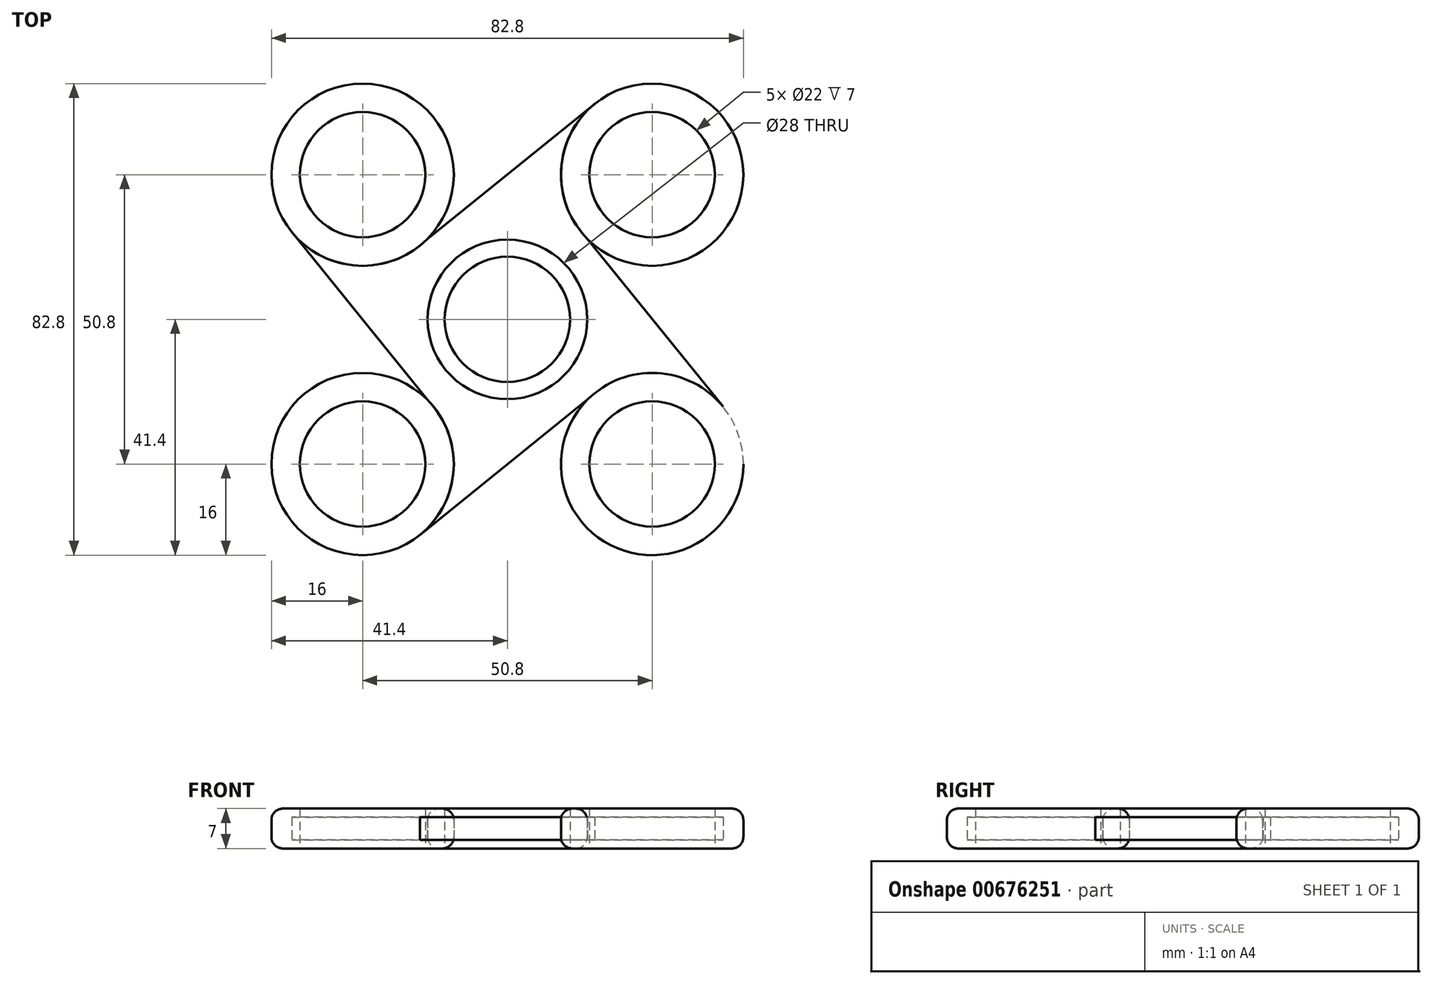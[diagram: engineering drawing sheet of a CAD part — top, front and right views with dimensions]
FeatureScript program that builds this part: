
annotation { "Feature Type Name" : "Feature", "Feature Type Description" : "" }
export const myFeature = defineFeature(function(context is Context, id is Id, definition is map)
    precondition{}
    {
        {
            var Q0;
            Q0=qCreatedBy(makeId("Top.planeOp"),FACE);
            var sketch = newSketch(context, id + "F0", { "sketchPlane" : qUnion([Q0])});
            skLineSegment(sketch, "E0.bottom", {"start": v(0, 0) * mm, "end": v(50.8, 0) * mm, "construction": true});
            skLineSegment(sketch, "E0.top", {"start": v(0, -50.8) * mm, "end": v(50.8, -50.8) * mm, "construction": true});
            skLineSegment(sketch, "E0.left", {"start": v(0, 0) * mm, "end": v(0, -50.8) * mm, "construction": true});
            skLineSegment(sketch, "E0.right", {"start": v(50.8, 0) * mm, "end": v(50.8, -50.8) * mm, "construction": true});
            skCircle(sketch, "E1", {"center": v(0, 0) * mm, "radius": 11 * mm});
            skCircle(sketch, "E2", {"center": v(50.8, 0) * mm, "radius": 11 * mm});
            skCircle(sketch, "E3", {"center": v(50.8, -50.8) * mm, "radius": 11 * mm});
            skCircle(sketch, "E4", {"center": v(0, -50.8) * mm, "radius": 11 * mm});
            skCircle(sketch, "E5", {"center": v(0, -50.8) * mm, "radius": 4 * mm});
            skCircle(sketch, "E6", {"center": v(0, 0) * mm, "radius": 4 * mm});
            skCircle(sketch, "E7", {"center": v(50.8, 0) * mm, "radius": 4 * mm});
            skCircle(sketch, "E8", {"center": v(50.8, -50.8) * mm, "radius": 4 * mm});
            skLineSegment(sketch, "E9", {"start": v(0, -50.8) * mm, "end": v(50.8, 0) * mm, "construction": true});
            skLineSegment(sketch, "E10", {"start": v(50.8, -50.8) * mm, "end": v(0, 0) * mm, "construction": true});
            skCircle(sketch, "E11", {"center": v(25.4, -25.4) * mm, "radius": 4 * mm});
            skCircle(sketch, "E12", {"center": v(25.4, -25.4) * mm, "radius": 11 * mm});
            skCircle(sketch, "E13", {"center": v(0, 0) * mm, "radius": 16 * mm});
            skCircle(sketch, "E14", {"center": v(50.8, 0) * mm, "radius": 16 * mm});
            skCircle(sketch, "E15", {"center": v(50.8, -50.8) * mm, "radius": 16 * mm});
            skCircle(sketch, "E16", {"center": v(0, -50.8) * mm, "radius": 16 * mm});
            skLineSegment(sketch, "E17", {"start": v(11.31, -11.31) * mm, "end": v(40.75, 12.45) * mm});
            skLineSegment(sketch, "E18", {"start": v(40.75, 12.45) * mm, "end": v(50.8, 0) * mm});
            skLineSegment(sketch, "E19", {"start": v(39.49, -11.31) * mm, "end": v(63.25, -40.75) * mm});
            skLineSegment(sketch, "E20", {"start": v(63.25, -40.75) * mm, "end": v(50.8, -50.8) * mm});
            skLineSegment(sketch, "E21", {"start": v(39.49, -39.49) * mm, "end": v(10.05, -63.25) * mm});
            skLineSegment(sketch, "E22", {"start": v(10.05, -63.25) * mm, "end": v(0, -50.8) * mm});
            skLineSegment(sketch, "E23", {"start": v(11.31, -39.49) * mm, "end": v(-12.45, -10.05) * mm});
            skLineSegment(sketch, "E24", {"start": v(-12.45, -10.05) * mm, "end": v(0, 0) * mm});
            skCircle(sketch, "E25", {"center": v(25.4, -25.4) * mm, "radius": 14 * mm});
            skSolve(sketch);
        }
        {
            var Q0;
            {var subQ5=sQuery(id+"F0.wireOp",EDGE,"E17");Q0=makeQuery(id+"F0.imprint","IMPRINT",FACE,{"disambiguationData":[TD([[makeQuery(id+"F0.imprint","IMPRINT",EDGE,{"derivedFrom":subQ5}),-1.0]])]});}
            extrude(context, id + "F1", {"entities" : qUnion([Q0]), "endBound" : BoundingType.SYMMETRIC, "depth" : 4 * mm, "offsetDistance" : 25 * mm});
        }
        {
            var Q0;
            Q0=makeQuery(id+"F0.imprint","IMPRINT",FACE,{"disambiguationData":[TD([[makeQuery(id+"F0.imprint","IMPRINT",EDGE,{"derivedFrom":sQuery(id+"F0.wireOp",EDGE,"E4")}),-1.0]])]});
            var Q1;
            Q1=makeQuery(id+"F0.imprint","IMPRINT",FACE,{"disambiguationData":[TD([[makeQuery(id+"F0.imprint","IMPRINT",EDGE,{"derivedFrom":sQuery(id+"F0.wireOp",EDGE,"E3")}),-1.0]])]});
            var Q2;
            Q2=makeQuery(id+"F0.imprint","IMPRINT",FACE,{"disambiguationData":[TD([[makeQuery(id+"F0.imprint","IMPRINT",EDGE,{"derivedFrom":sQuery(id+"F0.wireOp",EDGE,"E2")}),-1.0]])]});
            var Q3;
            Q3=makeQuery(id+"F0.imprint","IMPRINT",FACE,{"disambiguationData":[TD([[makeQuery(id+"F0.imprint","IMPRINT",EDGE,{"derivedFrom":sQuery(id+"F0.wireOp",EDGE,"E1")}),-1.0]])]});
            extrude(context, id + "F2", {"entities" : qUnion([Q0, Q1, Q2, Q3]), "endBound" : BoundingType.SYMMETRIC, "depth" : 7 * mm, "offsetDistance" : 25 * mm});
        }
        {
            var Q0;
            Q0=makeQuery(id+"F0.imprint","IMPRINT",FACE,{"disambiguationData":[TD([[makeQuery(id+"F0.imprint","IMPRINT",EDGE,{"derivedFrom":sQuery(id+"F0.wireOp",EDGE,"E12")}),-1.0]])]});
            extrude(context, id + "F3", {"entities" : qUnion([Q0]), "endBound" : BoundingType.SYMMETRIC, "depth" : 7 * mm, "offsetDistance" : 25 * mm});
        }
        {
            var Q0;
            Q0=makeQuery(id+"F2.opExtrude","CAP_EDGE",EDGE,{"disambiguationData":[OSD([sQuery(id+"F0.wireOp",EDGE,"E16")])],"isStart":false});
            var Q1;
            Q1=makeQuery(id+"F2.opExtrude","CAP_EDGE",EDGE,{"disambiguationData":[OSD([sQuery(id+"F0.wireOp",EDGE,"E15")])],"isStart":false});
            var Q2;
            Q2=makeQuery(id+"F2.opExtrude","CAP_EDGE",EDGE,{"disambiguationData":[OSD([sQuery(id+"F0.wireOp",EDGE,"E14")])],"isStart":false});
            var Q3;
            Q3=makeQuery(id+"F2.opExtrude","CAP_EDGE",EDGE,{"disambiguationData":[OSD([sQuery(id+"F0.wireOp",EDGE,"E13")])],"isStart":false});
            var Q4;
            Q4=makeQuery(id+"F3.opExtrude","CAP_EDGE",EDGE,{"disambiguationData":[OSD([sQuery(id+"F0.wireOp",EDGE,"E25")])],"isStart":false});
            var Q5;
            Q5=makeQuery(id+"F3.opExtrude","CAP_EDGE",EDGE,{"disambiguationData":[OSD([sQuery(id+"F0.wireOp",EDGE,"E25")])],"isStart":true});
            var Q6;
            Q6=makeQuery(id+"F2.opExtrude","CAP_EDGE",EDGE,{"disambiguationData":[OSD([sQuery(id+"F0.wireOp",EDGE,"E16")])],"isStart":true});
            var Q7;
            Q7=makeQuery(id+"F2.opExtrude","CAP_EDGE",EDGE,{"disambiguationData":[OSD([sQuery(id+"F0.wireOp",EDGE,"E15")])],"isStart":true});
            var Q8;
            Q8=makeQuery(id+"F2.opExtrude","CAP_EDGE",EDGE,{"disambiguationData":[OSD([sQuery(id+"F0.wireOp",EDGE,"E13")])],"isStart":true});
            var Q9;
            Q9=makeQuery(id+"F2.opExtrude","CAP_EDGE",EDGE,{"disambiguationData":[OSD([sQuery(id+"F0.wireOp",EDGE,"E14")])],"isStart":true});
            fillet(context, id + "F4", {"entities" : qUnion([Q0, Q1, Q2, Q3, Q4, Q5, Q6, Q7, Q8, Q9]), "radius" : 2 * mm, "tangentPropagation" : true, "allowEdgeOverflow" : false});
        }
    });
